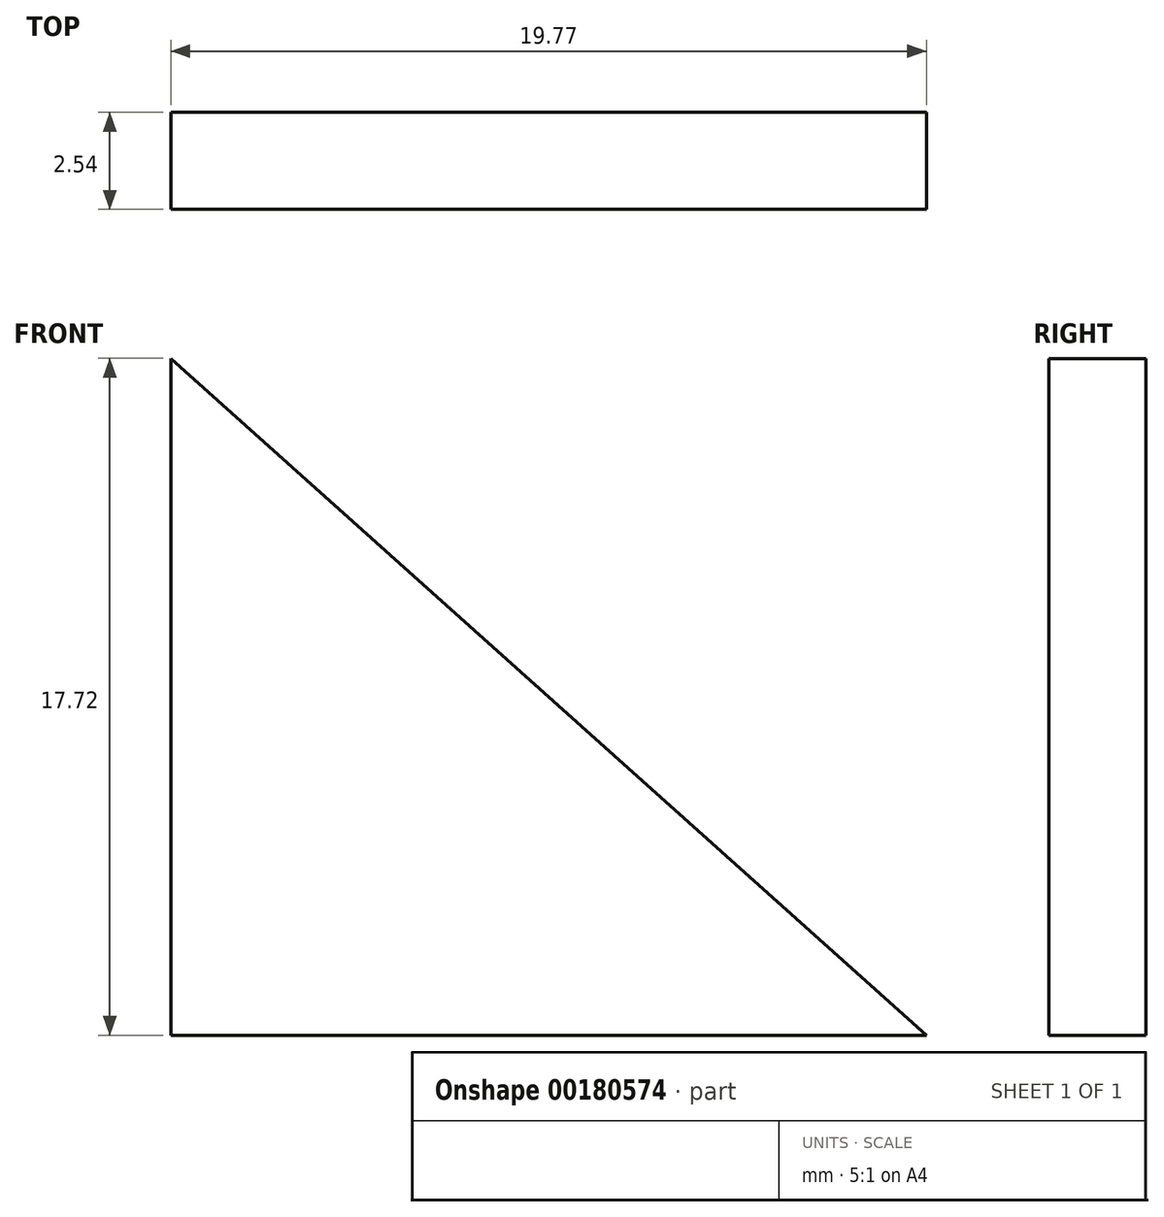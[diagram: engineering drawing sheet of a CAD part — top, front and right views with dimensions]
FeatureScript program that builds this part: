
annotation { "Feature Type Name" : "Feature", "Feature Type Description" : "" }
export const myFeature = defineFeature(function(context is Context, id is Id, definition is map)
    precondition{}
    {
        {
            var Q0;
            Q0=qCreatedBy(makeId("Front.planeOp"),FACE);
            var sketch = newSketch(context, id + "F0", { "sketchPlane" : qUnion([Q0])});
            skLineSegment(sketch, "E0", {"start": v(0, 0) * mm, "end": v(-19.77, 0) * mm});
            skLineSegment(sketch, "E1", {"start": v(-19.77, 0) * mm, "end": v(-19.77, 17.72) * mm});
            skLineSegment(sketch, "E2", {"start": v(-19.77, 17.72) * mm, "end": v(0, 0) * mm});
            skSolve(sketch);
        }
        {
            var Q0;
            Q0 = qSketchRegion(id + "F0", true);
            extrude(context, id + "F1", {"entities" : qUnion([Q0]), "depth" : 2.54 * mm});
        }
    });
